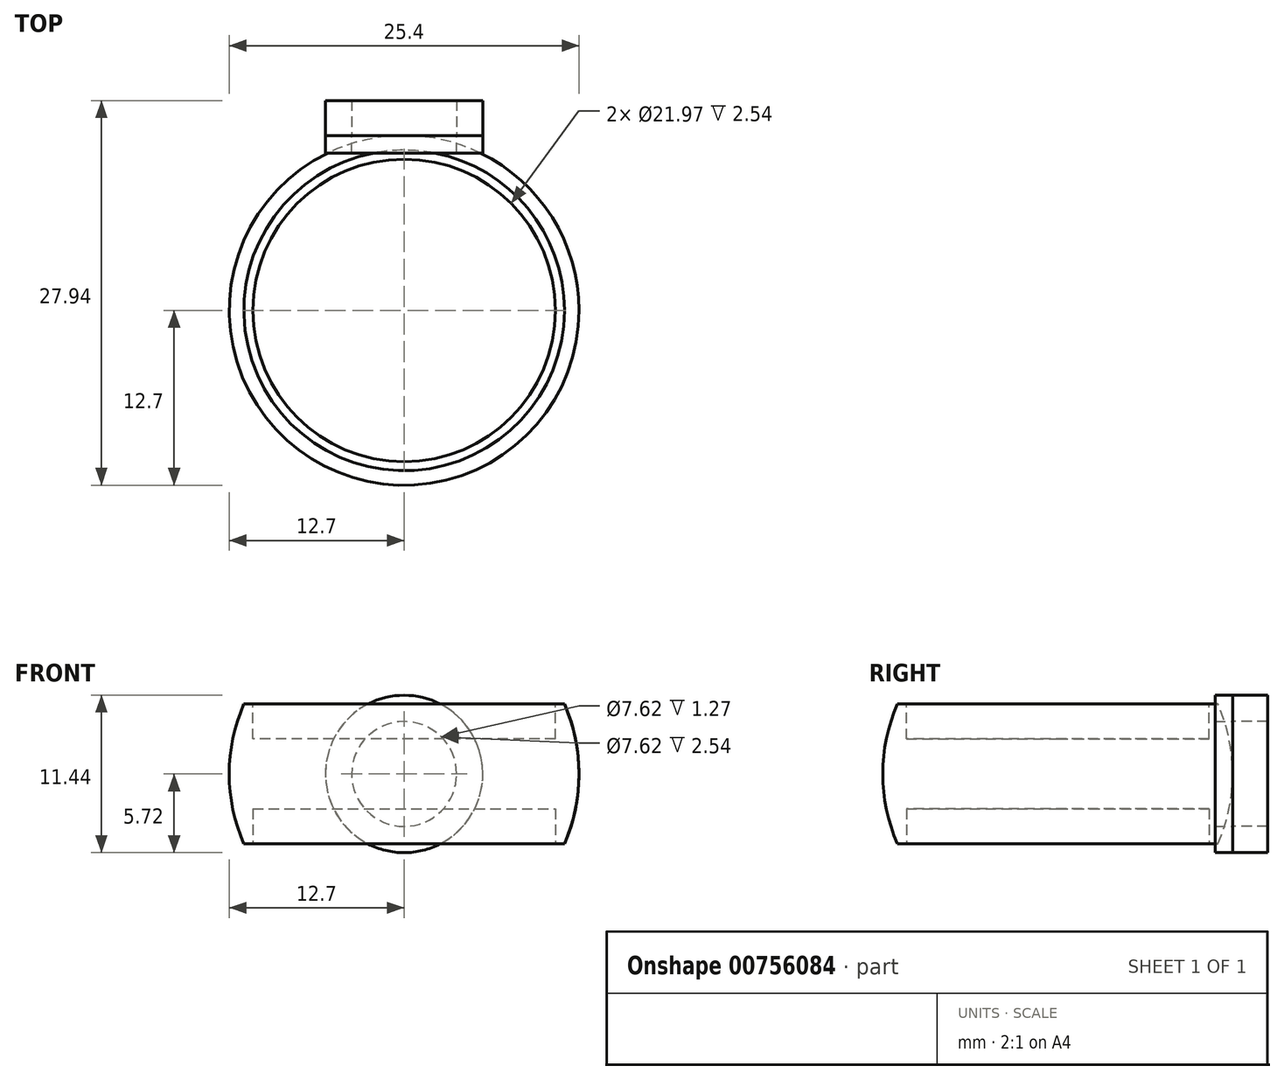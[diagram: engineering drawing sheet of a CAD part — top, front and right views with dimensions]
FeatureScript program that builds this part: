
annotation { "Feature Type Name" : "Feature", "Feature Type Description" : "" }
export const myFeature = defineFeature(function(context is Context, id is Id, definition is map)
    precondition{}
    {
        {
            var Q0;
            Q0=qCreatedBy(makeId("Right.planeOp"),FACE);
            var sketch = newSketch(context, id + "F0", { "sketchPlane" : qUnion([Q0])});
            skArc(sketch, "E0", {"start": v(-24.34, 5.08) * mm, "mid": v(-25.4, 0) * mm, "end": v(-24.34, -5.08) * mm});
            skLineSegment(sketch, "E1", {"start": v(-12.7, 5.08) * mm, "end": v(-24.34, 5.08) * mm});
            skLineSegment(sketch, "E2", {"start": v(-12.7, -5.08) * mm, "end": v(-24.34, -5.08) * mm});
            skLineSegment(sketch, "E3", {"start": v(-12.7, 5.08) * mm, "end": v(-12.7, -5.08) * mm});
            skSolve(sketch);
        }
        {
            var Q0;
            Q0=makeQuery(id+"F0.imprint","IMPRINT",FACE,{"disambiguationData":[TD([[makeQuery(id+"F0.imprint","IMPRINT",EDGE,{"derivedFrom":sQuery(id+"F0.wireOp",EDGE,"E0")}),1.0]])]});
            var Q1;
            Q1=sQuery(id+"F0.wireOp",EDGE,"E3");
            revolve(context, id + "F1", {"surfaceOperationType" : NewSurfaceOperationType.NEW, "entities" : qUnion([Q0]), "axis" : qUnion([Q1]), "revolveType" : RevolveType.FULL});
        }
        {
            var Q0;
            Q0=makeQuery(id+"F1.opRevolve","SWEPT_FACE",FACE,{"disambiguationData":[OSD([sQuery(id+"F0.wireOp",EDGE,"E1")])]});
            var sketch = newSketch(context, id + "F2", { "sketchPlane" : qUnion([Q0])});
            skCircle(sketch, "E4", {"center": v(0, -12.7) * mm, "radius": 10.99 * mm});
            skSolve(sketch);
        }
        {
            var Q0;
            Q0=makeQuery(id+"F2.imprint","IMPRINT",FACE,{"disambiguationData":[TD([[makeQuery(id+"F2.imprint","IMPRINT",EDGE,{"derivedFrom":sQuery(id+"F2.wireOp",EDGE,"E4")}),1.0]])]});
            extrude(context, id + "F3", {"entities" : qUnion([Q0]), "operationType" : NewBodyOperationType.REMOVE, "oppositeDirection" : true, "depth" : 2.54 * mm, "offsetDistance" : 25.4 * mm});
        }
        {
            var Q0;
            Q0=makeQuery(id+"F1.opRevolve","SWEPT_FACE",FACE,{"disambiguationData":[OSD([sQuery(id+"F0.wireOp",EDGE,"E2")])]});
            var sketch = newSketch(context, id + "F4", { "sketchPlane" : qUnion([Q0])});
            skCircle(sketch, "E5", {"center": v(0, 12.7) * mm, "radius": 10.99 * mm});
            skSolve(sketch);
        }
        {
            var Q0;
            Q0=makeQuery(id+"F4.imprint","IMPRINT",FACE,{"disambiguationData":[TD([[makeQuery(id+"F4.imprint","IMPRINT",EDGE,{"derivedFrom":sQuery(id+"F4.wireOp",EDGE,"E5")}),1.0]])]});
            extrude(context, id + "F5", {"entities" : qUnion([Q0]), "operationType" : NewBodyOperationType.REMOVE, "oppositeDirection" : true, "depth" : 2.54 * mm, "offsetDistance" : 25.4 * mm});
        }
        {
            var Q0;
            Q0=qCreatedBy(makeId("Front.planeOp"),FACE);
            var sketch = newSketch(context, id + "F6", { "sketchPlane" : qUnion([Q0])});
            skCircle(sketch, "E6", {"center": v(0, 0) * mm, "radius": 5.72 * mm});
            skCircle(sketch, "E7", {"center": v(0, 0) * mm, "radius": 3.81 * mm});
            skSolve(sketch);
        }
        {
            var Q0;
            Q0=makeQuery(id+"F6.imprint","IMPRINT",FACE,{"disambiguationData":[TD([[makeQuery(id+"F6.imprint","IMPRINT",EDGE,{"derivedFrom":sQuery(id+"F6.wireOp",EDGE,"E6")}),1.0]])]});
            extrude(context, id + "F7", {"entities" : qUnion([Q0]), "depth" : -2.54 * mm, "offsetDistance" : 25.4 * mm});
        }
        {
            var Q0;
            Q0=qCreatedBy(makeId("Front.planeOp"),FACE);
            var sketch = newSketch(context, id + "F8", { "sketchPlane" : qUnion([Q0])});
            skCircle(sketch, "E8", {"center": v(0, 0) * mm, "radius": 5.72 * mm});
            skCircle(sketch, "E9", {"center": v(0, 0) * mm, "radius": 3.81 * mm});
            skSolve(sketch);
        }
        {
            var Q0;
            Q0=makeQuery(id+"F8.imprint","IMPRINT",FACE,{"disambiguationData":[TD([[makeQuery(id+"F8.imprint","IMPRINT",EDGE,{"derivedFrom":sQuery(id+"F8.wireOp",EDGE,"E8")}),1.0]])]});
            extrude(context, id + "F9", {"entities" : qUnion([Q0]), "depth" : 1.27 * mm, "offsetDistance" : 25.4 * mm});
        }
    });
